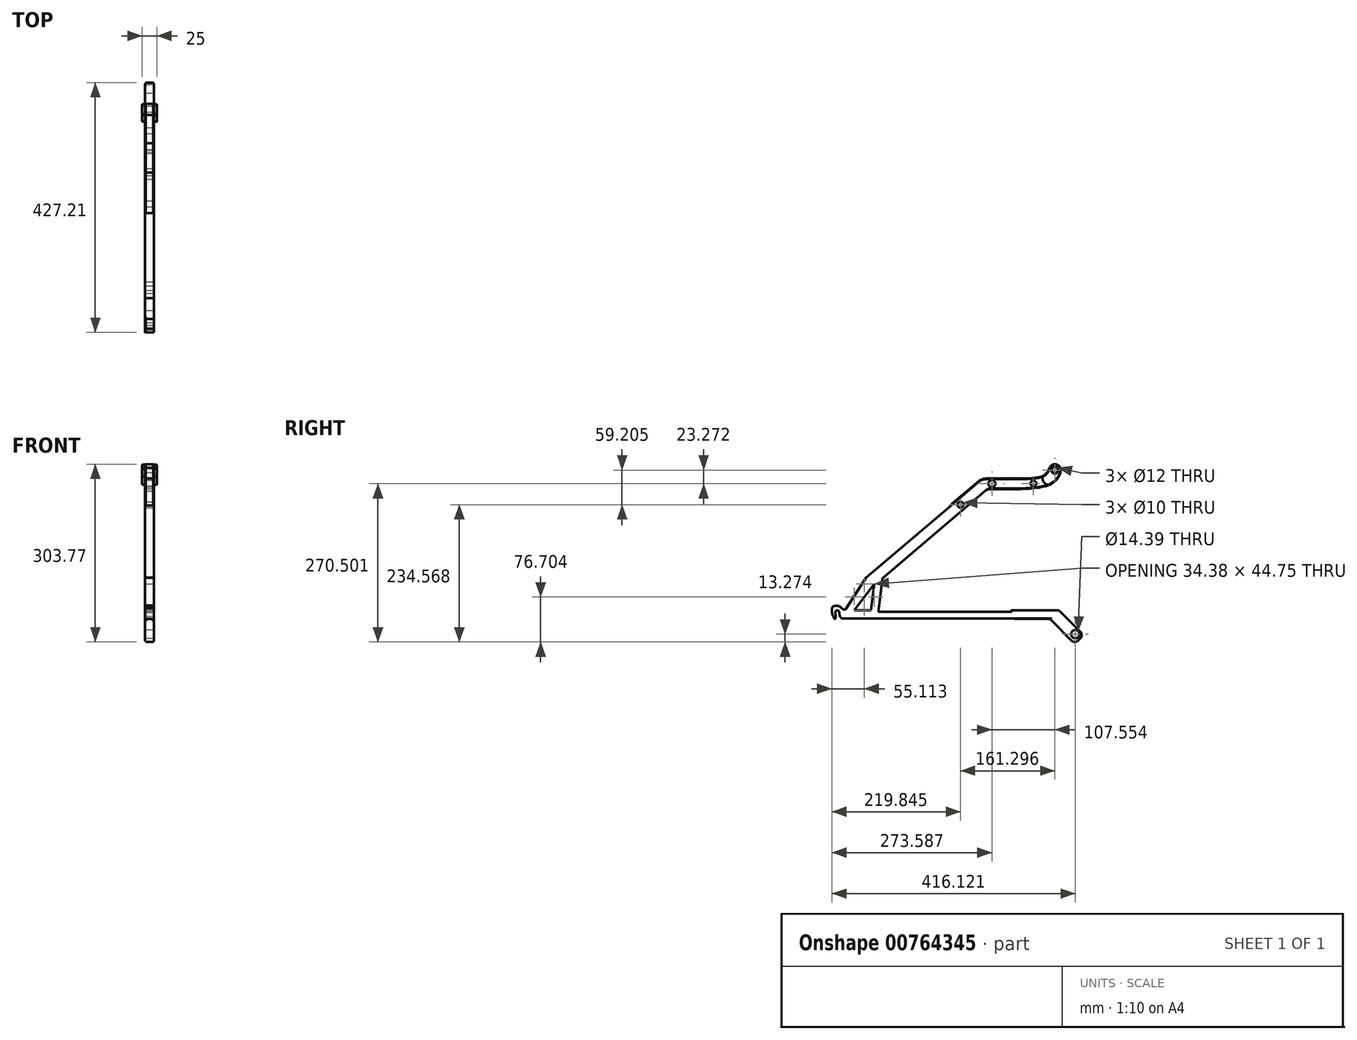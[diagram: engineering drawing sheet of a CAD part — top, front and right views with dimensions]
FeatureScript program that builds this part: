
annotation { "Feature Type Name" : "Feature", "Feature Type Description" : "" }
export const myFeature = defineFeature(function(context is Context, id is Id, definition is map)
    precondition{}
    {
        {
            var Q0;
            Q0=qCreatedBy(makeId("Right.planeOp"),FACE);
            var sketch = newSketch(context, id + "F0", { "sketchPlane" : qUnion([Q0])});
            skLineSegment(sketch, "E0", {"start": v(47.78, 0) * mm, "end": v(315.63, 0) * mm});
            skLineSegment(sketch, "E1", {"start": v(48.64, 41.27) * mm, "end": v(16.93, 0) * mm});
            skLineSegment(sketch, "E2", {"start": v(16.93, 0) * mm, "end": v(47.78, 0) * mm});
            skLineSegment(sketch, "E3.bottom", {"start": v(315.63, 0) * mm, "end": v(16.93, 0) * mm});
            skLineSegment(sketch, "E3.top", {"start": v(315.63, -15) * mm, "end": v(16.93, -15) * mm});
            skLineSegment(sketch, "E3.right", {"start": v(16.93, 0) * mm, "end": v(16.93, -15) * mm});
            skLineSegment(sketch, "E4.left", {"start": v(48.64, 41.27) * mm, "end": v(43.82, 0) * mm});
            skLineSegment(sketch, "E5", {"start": v(48.64, 41.27) * mm, "end": v(35.7, 56.52) * mm});
            skLineSegment(sketch, "E6", {"start": v(239.28, 203) * mm, "end": v(226.34, 218.25) * mm});
            skLineSegment(sketch, "E7", {"start": v(16.93, 0) * mm, "end": v(5.04, 9.14) * mm});
            skLineSegment(sketch, "E8", {"start": v(5.04, 9.14) * mm, "end": v(35.7, 56.52) * mm});
            skLineSegment(sketch, "E9", {"start": v(43.82, 0) * mm, "end": v(58.82, 0) * mm});
            skLineSegment(sketch, "E10", {"start": v(58.82, 0) * mm, "end": v(65.3, 55.4) * mm});
            skLineSegment(sketch, "E11", {"start": v(65.3, 55.4) * mm, "end": v(48.64, 41.27) * mm});
            skFitSpline(sketch, "E12", {"points": [v(226.34, 218.25) * mm, v(234.77, 223.82) * mm, v(251.34, 224.9) * mm], "startDerivative": vector(16.54, 14.26) * mm, "endDerivative": vector(26.5, -0.65) * mm});
            skFitSpline(sketch, "E13", {"points": [v(239.28, 203) * mm, v(245.05, 206.46) * mm, v(251.34, 206.86) * mm], "startDerivative": vector(8.53, 6.98) * mm, "endDerivative": vector(15.33, 0.96) * mm});
            skLineSegment(sketch, "E14.bottom", {"start": v(251.34, 224.9) * mm, "end": v(301.34, 224.9) * mm});
            skLineSegment(sketch, "E14.top", {"start": v(251.34, 206.86) * mm, "end": v(301.34, 206.86) * mm});
            skPoint(sketch, "E15", {"position": v(368.9, 239.44) * mm});
            skPoint(sketch, "E16", {"position": v(358.9, 249.44) * mm});
            skPoint(sketch, "E17", {"position": v(358.9, 229.44) * mm});
            skCircle(sketch, "E18", {"center": v(358.9, 239.44) * mm, "radius": 5 * mm});
            skFitSpline(sketch, "E19", {"points": [v(301.34, 206.86) * mm, v(354.55, 217) * mm, v(368.9, 239.44) * mm], "startDerivative": vector(106.9, 6.32) * mm, "endDerivative": vector(0.42, 60.1) * mm});
            skPoint(sketch, "E20", {"position": v(349.43, 242.67) * mm});
            skFitSpline(sketch, "E21", {"points": [v(301.34, 224.9) * mm, v(340.14, 230.35) * mm, v(349.43, 242.67) * mm], "startDerivative": vector(74.37, 2.6) * mm, "endDerivative": vector(12.8, 33.28) * mm});
            skArc(sketch, "E22", {"start": v(368.9, 239.44) * mm, "mid": v(360.53, 249.3) * mm, "end": v(349.43, 242.67) * mm});
            skCircle(sketch, "E23", {"center": v(322.28, 216.56) * mm, "radius": 5 * mm});
            skCircle(sketch, "E24", {"center": v(251.34, 216.17) * mm, "radius": 6 * mm});
            skLineSegment(sketch, "E25", {"start": v(16.93, -15) * mm, "end": v(5.04, -15) * mm});
            skLineSegment(sketch, "E26", {"start": v(5.04, -15) * mm, "end": v(5.04, 9.14) * mm});
            skLineSegment(sketch, "E27", {"start": v(315.63, -15) * mm, "end": v(315.63, 0) * mm});
            skLineSegment(sketch, "E28", {"start": v(315.63, 0) * mm, "end": v(365.63, 0) * mm});
            skLineSegment(sketch, "E29", {"start": v(365.63, 0) * mm, "end": v(365.63, -15) * mm});
            skLineSegment(sketch, "E30", {"start": v(365.63, -15) * mm, "end": v(315.63, -15) * mm});
            skPoint(sketch, "E31", {"position": v(350.63, -15) * mm});
            skLineSegment(sketch, "E32", {"start": v(365.63, 0) * mm, "end": v(408.06, -42.43) * mm});
            skLineSegment(sketch, "E33", {"start": v(350.63, -15) * mm, "end": v(393.06, -57.43) * mm});
            skLineSegment(sketch, "E34", {"start": v(393.06, -57.43) * mm, "end": v(408.06, -42.43) * mm});
            skPoint(sketch, "E35", {"position": v(358.63, -15) * mm});
            skPoint(sketch, "E36", {"position": v(365.63, -8) * mm});
            skPoint(sketch, "E37", {"position": v(386.84, -21.21) * mm});
            skPoint(sketch, "E38", {"position": v(371.84, -36.21) * mm});
            skLineSegment(sketch, "E39", {"start": v(371.84, -36.21) * mm, "end": v(386.84, -21.21) * mm});
            skCircle(sketch, "E40", {"center": v(393.87, -41.06) * mm, "radius": 7.2 * mm});
            skPoint(sketch, "E41", {"position": v(131.02, 137.39) * mm});
            skPoint(sketch, "E42", {"position": v(143.96, 122.14) * mm});
            skPoint(sketch, "E43", {"position": v(115.77, 124.45) * mm});
            skPoint(sketch, "E44", {"position": v(128.7, 109.2) * mm});
            skPoint(sketch, "E45", {"position": v(159.2, 135.07) * mm});
            skPoint(sketch, "E46", {"position": v(146.27, 150.33) * mm});
            skLineSegment(sketch, "E47", {"start": v(128.7, 109.2) * mm, "end": v(115.77, 124.45) * mm});
            skLineSegment(sketch, "E48", {"start": v(35.7, 56.52) * mm, "end": v(48.64, 41.27) * mm});
            skLineSegment(sketch, "E49", {"start": v(146.27, 150.33) * mm, "end": v(159.2, 135.07) * mm});
            skLineSegment(sketch, "E50", {"start": v(146.27, 150.33) * mm, "end": v(226.34, 218.25) * mm});
            skLineSegment(sketch, "E51", {"start": v(35.7, 56.52) * mm, "end": v(115.77, 124.45) * mm});
            skLineSegment(sketch, "E52", {"start": v(65.3, 55.4) * mm, "end": v(128.7, 109.2) * mm});
            skLineSegment(sketch, "E53", {"start": v(159.2, 135.07) * mm, "end": v(239.28, 203) * mm});
            skLineSegment(sketch, "E54", {"start": v(115.77, 124.45) * mm, "end": v(146.27, 150.33) * mm});
            skLineSegment(sketch, "E55", {"start": v(128.7, 109.2) * mm, "end": v(159.2, 135.07) * mm});
            skSolve(sketch);
        }
        {
            var Q0;
            {var subQ1=sQuery(id+"F0.wireOp",EDGE,"E6");Q0=makeQuery(id+"F0.imprint","IMPRINT",FACE,{"disambiguationData":[TD([[makeQuery(id+"F0.imprint","IMPRINT",EDGE,{"derivedFrom":subQ1}),1.0]])]});}
            var Q1;
            {var subQ1=sQuery(id+"F0.wireOp",EDGE,"E7");Q1=makeQuery(id+"F0.imprint","IMPRINT",FACE,{"disambiguationData":[TD([[makeQuery(id+"F0.imprint","IMPRINT",EDGE,{"derivedFrom":subQ1}),-1.0]])]});}
            var Q2;
            Q2=makeQuery(id+"F0.imprint","IMPRINT",FACE,{"disambiguationData":[TD([[makeQuery(id+"F0.imprint","IMPRINT",EDGE,{"derivedFrom":sQuery(id+"F0.wireOp",EDGE,"E3.right")}),-1.0]])]});
            var Q3;
            Q3=makeQuery(id+"F0.imprint","IMPRINT",FACE,{"disambiguationData":[TD([[makeQuery(id+"F0.imprint","IMPRINT",EDGE,{"derivedFrom":sQuery(id+"F0.wireOp",EDGE,"E3.top")}),-1.0]])]});
            var Q4;
            {var subQ0=sQuery(id+"F0.wireOp",EDGE,"E4.left");Q4=makeQuery(id+"F0.imprint","IMPRINT",FACE,{"disambiguationData":[TD([[makeQuery(id+"F0.imprint","IMPRINT",EDGE,{"derivedFrom":subQ0}),1.0]])]});}
            var Q5;
            {var subQ3=sQuery(id+"F0.wireOp",EDGE,"RTDkQwoI-wCG5-Ql9m-PHR5-vW7OaOIPGGAD.top");Q5=makeQuery(id+"F0.imprint","IMPRINT",FACE,{"disambiguationData":[TD([[makeQuery(id+"F0.imprint","IMPRINT",EDGE,{"derivedFrom":subQ3}),-1.0]])]});}
            var Q6;
            {var subQ1=sQuery(id+"F0.wireOp",EDGE,"E1");var subQ3=sQuery(id+"F0.wireOp",EDGE,"RTDkQwoI-wCG5-Ql9m-PHR5-vW7OaOIPGGAD.left");var subQ4=makeQuery(id+"F0.imprint","INTERSECT",VERTEX,{"derivedFrom":[subQ1,subQ3]});Q6=makeQuery(id+"F0.imprint","IMPRINT",FACE,{"disambiguationData":[TD([[makeQuery(id+"F0.imprint","IMPRINT",EDGE,{"disambiguationData":[TD([[subQ4,-1.0]])],"derivedFrom":subQ3}),-1.0]])]});}
            var Q7;
            {var subQ0=sQuery(id+"F0.wireOp",EDGE,"o3pL6dEJ-hwyi-6mrB-k6X7-aminsl83ahjA");Q7=makeQuery(id+"F0.imprint","IMPRINT",FACE,{"disambiguationData":[TD([[makeQuery(id+"F0.imprint","IMPRINT",EDGE,{"derivedFrom":subQ0}),-1.0]])]});}
            var Q8;
            {var subQ0=sQuery(id+"F0.wireOp",EDGE,"o3pL6dEJ-hwyi-6mrB-k6X7-aminsl83ahjA");Q8=makeQuery(id+"F0.imprint","IMPRINT",FACE,{"disambiguationData":[TD([[makeQuery(id+"F0.imprint","IMPRINT",EDGE,{"derivedFrom":subQ0}),1.0]])]});}
            var Q9;
            Q9=makeQuery(id+"F0.imprint","IMPRINT",FACE,{"disambiguationData":[TD([[makeQuery(id+"F0.imprint","IMPRINT",EDGE,{"derivedFrom":sQuery(id+"F0.wireOp",EDGE,"E6")}),-1.0]])]});
            var Q10;
            Q10=makeQuery(id+"F0.imprint","IMPRINT",FACE,{"disambiguationData":[TD([[makeQuery(id+"F0.imprint","IMPRINT",EDGE,{"derivedFrom":sQuery(id+"F0.wireOp",EDGE,"E14.bottom")}),-1.0]])]});
            var Q11;
            Q11=makeQuery(id+"F0.imprint","IMPRINT",FACE,{"disambiguationData":[TD([[makeQuery(id+"F0.imprint","IMPRINT",EDGE,{"derivedFrom":sQuery(id+"F0.wireOp",EDGE,"E14.right")}),1.0]])]});
            var Q12;
            {var subQ0=sQuery(id+"F0.wireOp",EDGE,"E3.right");Q12=makeQuery(id+"F0.imprint","IMPRINT",FACE,{"disambiguationData":[TD([[makeQuery(id+"F0.imprint","IMPRINT",EDGE,{"derivedFrom":subQ0}),1.0]])]});}
            var Q13;
            {var subQ3=sQuery(id+"F0.wireOp",EDGE,"hnlP5vd8-Fwl7-W3YU-HfNq-rofw2tE7fOju");Q13=makeQuery(id+"F0.imprint","IMPRINT",FACE,{"disambiguationData":[TD([[makeQuery(id+"F0.imprint","IMPRINT",EDGE,{"derivedFrom":subQ3}),-1.0]])]});}
            var Q14;
            {var subQ4=sQuery(id+"F0.wireOp",EDGE,"zAPuBMNa-KC0v-FcAM-JJp2-Pc91iyWnGTPB");Q14=makeQuery(id+"F0.imprint","IMPRINT",FACE,{"disambiguationData":[TD([[makeQuery(id+"F0.imprint","IMPRINT",EDGE,{"derivedFrom":subQ4}),-1.0]])]});}
            var Q15;
            {var subQ0=sQuery(id+"F0.wireOp",EDGE,"E3.left");Q15=makeQuery(id+"F0.imprint","IMPRINT",FACE,{"disambiguationData":[TD([[makeQuery(id+"F0.imprint","IMPRINT",EDGE,{"derivedFrom":subQ0}),1.0]])]});}
            var Q16;
            Q16=makeQuery(id+"F0.imprint","IMPRINT",FACE,{"disambiguationData":[TD([[makeQuery(id+"F0.imprint","IMPRINT",EDGE,{"derivedFrom":sQuery(id+"F0.wireOp",EDGE,"E27")}),-1.0]])]});
            var Q17;
            {var subQ2=sQuery(id+"F0.wireOp",EDGE,"E29");Q17=makeQuery(id+"F0.imprint","IMPRINT",FACE,{"disambiguationData":[TD([[makeQuery(id+"F0.imprint","IMPRINT",EDGE,{"derivedFrom":subQ2}),1.0]])]});}
            var Q18;
            {var subQ0=sQuery(id+"F0.wireOp",EDGE,"E33");var subQ1=sQuery(id+"F0.wireOp",EDGE,"E30");var subQ2=makeQuery(id+"F0.imprint","INTERSECT",VERTEX,{"derivedFrom":[subQ1,subQ0]});Q18=makeQuery(id+"F0.imprint","IMPRINT",FACE,{"disambiguationData":[TD([[makeQuery(id+"F0.imprint","IMPRINT",EDGE,{"disambiguationData":[TD([[subQ2,-1.0]])],"derivedFrom":subQ0}),1.0]])]});}
            var Q19;
            {var subQ5=sQuery(id+"F0.wireOp",EDGE,"E34");Q19=makeQuery(id+"F0.imprint","IMPRINT",FACE,{"disambiguationData":[TD([[makeQuery(id+"F0.imprint","IMPRINT",EDGE,{"derivedFrom":subQ5}),1.0]])]});}
            var Q20;
            Q20=makeQuery(id+"F0.imprint","IMPRINT",FACE,{"disambiguationData":[TD([[makeQuery(id+"F0.imprint","IMPRINT",EDGE,{"derivedFrom":sQuery(id+"F0.wireOp",EDGE,"E11")}),-1.0]])]});
            var Q21;
            Q21=makeQuery(id+"F0.imprint","IMPRINT",FACE,{"disambiguationData":[TD([[makeQuery(id+"F0.imprint","IMPRINT",EDGE,{"derivedFrom":sQuery(id+"F0.wireOp",EDGE,"E49")}),1.0]])]});
            var Q22;
            Q22=makeQuery(id+"F0.imprint","IMPRINT",FACE,{"disambiguationData":[TD([[makeQuery(id+"F0.imprint","IMPRINT",EDGE,{"derivedFrom":sQuery(id+"F0.wireOp",EDGE,"E47")}),-1.0]])]});
            extrude(context, id + "F1", {"entities" : qUnion([Q0, Q1, Q2, Q3, Q4, Q5, Q6, Q7, Q8, Q9, Q10, Q11, Q12, Q13, Q14, Q15, Q16, Q17, Q18, Q19, Q20, Q21, Q22]), "depth" : 15 * mm, "offsetDistance" : 25 * mm});
        }
        {
            var Q0;
            {var subQ0=sQuery(id+"F0.wireOp",EDGE,"E3.bottom");Q0=makeQuery(id+"F1.opExtrude","CAP_EDGE",EDGE,{"disambiguationData":[OSD([subQ0]),TDD([makeQuery(id+"F0.imprint","IMPRINT",EDGE,{"disambiguationData":[TD([[makeQuery(id+"F0.imprint","INTERSECT",VERTEX,{"derivedFrom":[subQ0,sQuery(id+"F0.wireOp",EDGE,"E3.left")]}),-1.0]])],"derivedFrom":subQ0})])],"isStart":false});}
            var Q1;
            {var subQ0=sQuery(id+"F0.wireOp",EDGE,"E3.bottom");Q1=makeQuery(id+"F1.opExtrude","CAP_EDGE",EDGE,{"disambiguationData":[OSD([subQ0]),TDD([makeQuery(id+"F0.imprint","IMPRINT",EDGE,{"disambiguationData":[TD([[makeQuery(id+"F0.imprint","INTERSECT",VERTEX,{"derivedFrom":[subQ0,sQuery(id+"F0.wireOp",EDGE,"E3.left")]}),-1.0]])],"derivedFrom":subQ0})])],"isStart":true});}
            var Q2;
            Q2=makeQuery(id+"F1.opExtrude","CAP_EDGE",EDGE,{"disambiguationData":[OSD([sQuery(id+"F0.wireOp",EDGE,"E3.top")])],"isStart":true});
            var Q3;
            Q3=makeQuery(id+"F1.opExtrude","CAP_EDGE",EDGE,{"disambiguationData":[OSD([sQuery(id+"F0.wireOp",EDGE,"E3.top")])],"isStart":false});
            var Q4;
            Q4=makeQuery(id+"F1.opExtrude","CAP_EDGE",EDGE,{"disambiguationData":[OSD([sQuery(id+"F0.wireOp",EDGE,"E3.left")])],"isStart":false});
            var Q5;
            Q5=makeQuery(id+"F1.opExtrude","SWEPT_EDGE",EDGE,{"disambiguationData":[OSD([sQuery(id+"F0.wireOp",EDGE,"E3.bottom"),sQuery(id+"F0.wireOp",EDGE,"E3.left")])]});
            var Q6;
            Q6=makeQuery(id+"F1.opExtrude","CAP_EDGE",EDGE,{"disambiguationData":[OSD([sQuery(id+"F0.wireOp",EDGE,"E3.left")])],"isStart":true});
            var Q7;
            Q7=makeQuery(id+"F1.opExtrude","SWEPT_EDGE",EDGE,{"disambiguationData":[OSD([sQuery(id+"F0.wireOp",EDGE,"E3.top"),sQuery(id+"F0.wireOp",EDGE,"E3.left")])]});
            var Q8;
            Q8=makeQuery(id+"F1.opExtrude","CAP_EDGE",EDGE,{"disambiguationData":[OSD([sQuery(id+"F0.wireOp",EDGE,"d41c5ef0-c10e-4e75-b374-802d414c0d57")])],"isStart":false});
            var Q9;
            Q9=makeQuery(id+"F1.opExtrude","CAP_EDGE",EDGE,{"disambiguationData":[OSD([sQuery(id+"F0.wireOp",EDGE,"d41c5ef0-c10e-4e75-b374-802d414c0d57")])],"isStart":true});
            var Q10;
            Q10=makeQuery(id+"F1.opExtrude","CAP_EDGE",EDGE,{"disambiguationData":[OSD([sQuery(id+"F0.wireOp",EDGE,"E1")])],"isStart":false});
            var Q11;
            Q11=makeQuery(id+"F1.opExtrude","CAP_EDGE",EDGE,{"disambiguationData":[OSD([sQuery(id+"F0.wireOp",EDGE,"E4.left")])],"isStart":false});
            var Q12;
            {var subQ0=sQuery(id+"F0.wireOp",EDGE,"E3.bottom");Q12=makeQuery(id+"F1.opExtrude","CAP_EDGE",EDGE,{"disambiguationData":[OSD([subQ0]),TDD([makeQuery(id+"F0.imprint","IMPRINT",EDGE,{"disambiguationData":[TD([[makeQuery(id+"F0.imprint","INTERSECT",VERTEX,{"derivedFrom":[subQ0,sQuery(id+"F0.wireOp",EDGE,"E4.left"),sQuery(id+"F0.wireOp",EDGE,"E9")]}),-1.0]])],"derivedFrom":subQ0})])],"isStart":false});}
            var Q13;
            Q13=makeQuery(id+"F1.opExtrude","CAP_EDGE",EDGE,{"disambiguationData":[OSD([sQuery(id+"F0.wireOp",EDGE,"E10")])],"isStart":false});
            var Q14;
            Q14=makeQuery(id+"F1.opExtrude","CAP_EDGE",EDGE,{"disambiguationData":[OSD([sQuery(id+"F0.wireOp",EDGE,"E8")])],"isStart":false});
            var Q15;
            Q15=makeQuery(id+"F1.opExtrude","CAP_EDGE",EDGE,{"disambiguationData":[OSD([sQuery(id+"F0.wireOp",EDGE,"E8")])],"isStart":true});
            var Q16;
            Q16=makeQuery(id+"F1.opExtrude","CAP_EDGE",EDGE,{"disambiguationData":[OSD([sQuery(id+"F0.wireOp",EDGE,"E1")])],"isStart":true});
            var Q17;
            Q17=makeQuery(id+"F1.opExtrude","CAP_EDGE",EDGE,{"disambiguationData":[OSD([sQuery(id+"F0.wireOp",EDGE,"E4.left")])],"isStart":true});
            var Q18;
            {var subQ0=sQuery(id+"F0.wireOp",EDGE,"E3.bottom");Q18=makeQuery(id+"F1.opExtrude","CAP_EDGE",EDGE,{"disambiguationData":[OSD([subQ0]),TDD([makeQuery(id+"F0.imprint","IMPRINT",EDGE,{"disambiguationData":[TD([[makeQuery(id+"F0.imprint","INTERSECT",VERTEX,{"derivedFrom":[subQ0,sQuery(id+"F0.wireOp",EDGE,"E4.left"),sQuery(id+"F0.wireOp",EDGE,"E9")]}),-1.0]])],"derivedFrom":subQ0})])],"isStart":true});}
            var Q19;
            Q19=makeQuery(id+"F1.opExtrude","CAP_EDGE",EDGE,{"disambiguationData":[OSD([sQuery(id+"F0.wireOp",EDGE,"E10")])],"isStart":true});
            var Q20;
            Q20=makeQuery(id+"F1.opExtrude","CAP_EDGE",EDGE,{"disambiguationData":[OSD([sQuery(id+"F0.wireOp",EDGE,"uIqcDY9T-Jbxf-aRt4-gg0R-6jHuYA81VSVm")])],"isStart":true});
            var Q21;
            Q21=makeQuery(id+"F1.opExtrude","CAP_EDGE",EDGE,{"disambiguationData":[OSD([sQuery(id+"F0.wireOp",EDGE,"uIqcDY9T-Jbxf-aRt4-gg0R-6jHuYA81VSVm")])],"isStart":false});
            var Q22;
            Q22=makeQuery(id+"F1.opExtrude","CAP_EDGE",EDGE,{"disambiguationData":[OSD([sQuery(id+"F0.wireOp",EDGE,"rEmcZTTS-8Wlh-duEK-OSmW-KXRGUTnN0HfS")])],"isStart":true});
            var Q23;
            Q23=makeQuery(id+"F1.opExtrude","CAP_EDGE",EDGE,{"disambiguationData":[OSD([sQuery(id+"F0.wireOp",EDGE,"rEmcZTTS-8Wlh-duEK-OSmW-KXRGUTnN0HfS")])],"isStart":false});
            var Q24;
            Q24=makeQuery(id+"F1.opExtrude","CAP_EDGE",EDGE,{"disambiguationData":[OSD([sQuery(id+"F0.wireOp",EDGE,"E12")])],"isStart":false});
            var Q25;
            Q25=makeQuery(id+"F1.opExtrude","CAP_EDGE",EDGE,{"disambiguationData":[OSD([sQuery(id+"F0.wireOp",EDGE,"E12")])],"isStart":true});
            var Q26;
            Q26=makeQuery(id+"F1.opExtrude","CAP_EDGE",EDGE,{"disambiguationData":[OSD([sQuery(id+"F0.wireOp",EDGE,"E14.bottom")])],"isStart":false});
            var Q27;
            Q27=makeQuery(id+"F1.opExtrude","CAP_EDGE",EDGE,{"disambiguationData":[OSD([sQuery(id+"F0.wireOp",EDGE,"E14.bottom")])],"isStart":true});
            var Q28;
            Q28=makeQuery(id+"F1.opExtrude","CAP_EDGE",EDGE,{"disambiguationData":[OSD([sQuery(id+"F0.wireOp",EDGE,"E21")])],"isStart":false});
            var Q29;
            Q29=makeQuery(id+"F1.opExtrude","CAP_EDGE",EDGE,{"disambiguationData":[OSD([sQuery(id+"F0.wireOp",EDGE,"E21")])],"isStart":true});
            var Q30;
            Q30=makeQuery(id+"F1.opExtrude","CAP_EDGE",EDGE,{"disambiguationData":[OSD([sQuery(id+"F0.wireOp",EDGE,"E13")])],"isStart":false});
            var Q31;
            Q31=makeQuery(id+"F1.opExtrude","CAP_EDGE",EDGE,{"disambiguationData":[OSD([sQuery(id+"F0.wireOp",EDGE,"E14.top")])],"isStart":false});
            var Q32;
            Q32=makeQuery(id+"F1.opExtrude","CAP_EDGE",EDGE,{"disambiguationData":[OSD([sQuery(id+"F0.wireOp",EDGE,"E19")])],"isStart":false});
            var Q33;
            Q33=makeQuery(id+"F1.opExtrude","CAP_EDGE",EDGE,{"disambiguationData":[OSD([sQuery(id+"F0.wireOp",EDGE,"E22")])],"isStart":false});
            var Q34;
            Q34=makeQuery(id+"F1.opExtrude","CAP_EDGE",EDGE,{"disambiguationData":[OSD([sQuery(id+"F0.wireOp",EDGE,"E18")])],"isStart":false});
            var Q35;
            Q35=makeQuery(id+"F1.opExtrude","CAP_EDGE",EDGE,{"disambiguationData":[OSD([sQuery(id+"F0.wireOp",EDGE,"E22")])],"isStart":true});
            var Q36;
            Q36=makeQuery(id+"F1.opExtrude","CAP_EDGE",EDGE,{"disambiguationData":[OSD([sQuery(id+"F0.wireOp",EDGE,"E18")])],"isStart":true});
            var Q37;
            Q37=makeQuery(id+"F1.opExtrude","CAP_EDGE",EDGE,{"disambiguationData":[OSD([sQuery(id+"F0.wireOp",EDGE,"E19")])],"isStart":true});
            var Q38;
            Q38=makeQuery(id+"F1.opExtrude","CAP_EDGE",EDGE,{"disambiguationData":[OSD([sQuery(id+"F0.wireOp",EDGE,"E14.top")])],"isStart":true});
            var Q39;
            Q39=makeQuery(id+"F1.opExtrude","CAP_EDGE",EDGE,{"disambiguationData":[OSD([sQuery(id+"F0.wireOp",EDGE,"E13")])],"isStart":true});
            chamfer(context, id + "F2", {"entities" : qUnion([Q0, Q1, Q2, Q3, Q4, Q5, Q6, Q7, Q8, Q9, Q10, Q11, Q12, Q13, Q14, Q15, Q16, Q17, Q18, Q19, Q20, Q21, Q22, Q23, Q24, Q25, Q26, Q27, Q28, Q29, Q30, Q31, Q32, Q33, Q34, Q35, Q36, Q37, Q38, Q39]), "width" : 1 * mm, "tangentPropagation" : true});
        }
        {
            var Q0;
            Q0=makeQuery(id+"F1.opExtrude","SWEPT_EDGE",EDGE,{"disambiguationData":[OSD([sQuery(id+"F0.wireOp",EDGE,"E3.bottom"),sQuery(id+"F0.wireOp",EDGE,"E9"),sQuery(id+"F0.wireOp",EDGE,"E10")])]});
            var Q1;
            Q1=makeQuery(id+"F1.opExtrude","SWEPT_EDGE",EDGE,{"disambiguationData":[OSD([sQuery(id+"F0.wireOp",EDGE,"uIqcDY9T-Jbxf-aRt4-gg0R-6jHuYA81VSVm"),sQuery(id+"F0.wireOp",EDGE,"E10"),sQuery(id+"F0.wireOp",EDGE,"E11")])]});
            fillet(context, id + "F3", {"entities" : qUnion([Q0, Q1]), "radius" : 2 * mm, "tangentPropagation" : true, "allowEdgeOverflow" : false});
        }
        {
            var Q0;
            Q0=makeQuery(id+"F1.opExtrude","SWEPT_EDGE",EDGE,{"disambiguationData":[OSD([sQuery(id+"F0.wireOp",EDGE,"E3.bottom"),sQuery(id+"F0.wireOp",EDGE,"E4.left"),sQuery(id+"F0.wireOp",EDGE,"E9")])]});
            var Q1;
            Q1=makeQuery(id+"F1.opExtrude","SWEPT_EDGE",EDGE,{"disambiguationData":[OSD([sQuery(id+"F0.wireOp",EDGE,"E1"),sQuery(id+"F0.wireOp",EDGE,"E3.bottom"),sQuery(id+"F0.wireOp",EDGE,"E3.right"),sQuery(id+"F0.wireOp",EDGE,"E7")])]});
            var Q2;
            Q2=makeQuery(id+"F1.opExtrude","SWEPT_EDGE",EDGE,{"disambiguationData":[OSD([sQuery(id+"F0.wireOp",EDGE,"E1"),sQuery(id+"F0.wireOp",EDGE,"E4.left"),sQuery(id+"F0.wireOp",EDGE,"E5"),sQuery(id+"F0.wireOp",EDGE,"E11")])]});
            fillet(context, id + "F4", {"entities" : qUnion([Q0, Q1, Q2]), "radius" : 1 * mm, "tangentPropagation" : true, "allowEdgeOverflow" : false});
        }
        {
            var Q0;
            Q0=makeQuery(id+"F1.opExtrude","SWEPT_FACE",FACE,{"disambiguationData":[OSD([sQuery(id+"F0.wireOp",EDGE,"E26")])]});
            var sketch = newSketch(context, id + "F5", { "sketchPlane" : qUnion([Q0])});
            skLineSegment(sketch, "E56.bottom", {"start": v(0, -15) * mm, "end": v(15, -15) * mm});
            skLineSegment(sketch, "E56.top", {"start": v(0, 9.14) * mm, "end": v(15, 9.14) * mm});
            skLineSegment(sketch, "E56.left", {"start": v(0, -15) * mm, "end": v(0, 9.14) * mm});
            skLineSegment(sketch, "E56.right", {"start": v(15, -15) * mm, "end": v(15, 9.14) * mm});
            skSolve(sketch);
        }
        {
            var Q0;
            Q0 = qSketchRegion(id + "F5", true);
            extrude(context, id + "F6", {"entities" : qUnion([Q0]), "operationType" : NewBodyOperationType.ADD, "depth" : 35 * mm, "offsetDistance" : 25 * mm});
        }
        {
            var Q0;
            Q0=makeQuery(id+"F6.boolean.opBoolean","MERGE",FACE,{"derivedFrom":[makeQuery(id+"F2.opChamfer","SPLIT",FACE,{"disambiguationData":[OD(0.0)],"derivedFrom":makeQuery(id+"F1.opExtrude","CAP_FACE",FACE,{"disambiguationData":[OSD([sQuery(id+"F0.wireOp",EDGE,"uIqcDY9T-Jbxf-aRt4-gg0R-6jHuYA81VSVm"),sQuery(id+"F0.wireOp",EDGE,"E1"),sQuery(id+"F0.wireOp",EDGE,"E3.bottom"),sQuery(id+"F0.wireOp",EDGE,"E3.top"),sQuery(id+"F0.wireOp",EDGE,"E3.left"),sQuery(id+"F0.wireOp",EDGE,"E4.left"),sQuery(id+"F0.wireOp",EDGE,"rEmcZTTS-8Wlh-duEK-OSmW-KXRGUTnN0HfS"),sQuery(id+"F0.wireOp",EDGE,"E8"),sQuery(id+"F0.wireOp",EDGE,"E10"),sQuery(id+"F0.wireOp",EDGE,"E12"),sQuery(id+"F0.wireOp",EDGE,"E13"),sQuery(id+"F0.wireOp",EDGE,"E14.bottom"),sQuery(id+"F0.wireOp",EDGE,"E14.top"),sQuery(id+"F0.wireOp",EDGE,"E18"),sQuery(id+"F0.wireOp",EDGE,"E19"),sQuery(id+"F0.wireOp",EDGE,"E21"),sQuery(id+"F0.wireOp",EDGE,"E22"),sQuery(id+"F0.wireOp",EDGE,"E23"),sQuery(id+"F0.wireOp",EDGE,"E24"),sQuery(id+"F0.wireOp",EDGE,"E25"),sQuery(id+"F0.wireOp",EDGE,"E26")])],"isStart":false})}),makeQuery(id+"F6.opExtrude","SWEPT_FACE",FACE,{"disambiguationData":[OSD([sQuery(id+"F5.wireOp",EDGE,"E56.right")])]})]});
            var sketch = newSketch(context, id + "F7", { "sketchPlane" : qUnion([Q0])});
            skLineSegment(sketch, "E57", {"start": v(5.04, 7.3) * mm, "end": v(1.23, 1.42) * mm});
            skPoint(sketch, "E58", {"position": v(-15.29, -15) * mm});
            skPoint(sketch, "E59", {"position": v(-8.29, -15) * mm});
            skFitSpline(sketch, "E60", {"points": [v(-15.81, -10.33) * mm, v(-16.74, -15) * mm, v(-20.68, -11.17) * mm], "startDerivative": vector(3.5, -16.33) * mm, "endDerivative": vector(-10.01, 17.22) * mm});
            skArc(sketch, "E61", {"start": v(-9.8, -2.74) * mm, "mid": v(-13.78, -0.75) * mm, "end": v(-16.49, -4.3) * mm});
            skFitSpline(sketch, "E62", {"points": [v(-23.08, 0.68) * mm, v(-23.08, -3.12) * mm, v(-20.68, -11.17) * mm], "startDerivative": vector(0.94, -17.18) * mm, "endDerivative": vector(7.79, -14.34) * mm});
            skLineSegment(sketch, "E63", {"start": v(-16.49, -4.3) * mm, "end": v(-15.81, -10.33) * mm});
            skFitSpline(sketch, "E64", {"points": [v(-9.8, -2.74) * mm, v(-6.92, -12.83) * mm, v(5.04, -15) * mm], "startDerivative": vector(3.63, -23.4) * mm, "endDerivative": vector(29.15, 0) * mm});
            skArc(sketch, "E65", {"start": v(-15.82, 7.7) * mm, "mid": v(-20.83, 5.61) * mm, "end": v(-23.08, 0.68) * mm});
            skFitSpline(sketch, "E66", {"points": [v(1.23, 1.42) * mm, v(-6.2, 4.2) * mm, v(-15.82, 7.7) * mm], "startDerivative": vector(-16.53, -11.89) * mm, "endDerivative": vector(-29.61, -1.65) * mm});
            skLineSegment(sketch, "E67", {"start": v(5.04, 7.3) * mm, "end": v(5.04, -15) * mm});
            skSolve(sketch);
        }
        {
            var Q0;
            Q0=makeQuery(id+"F7.imprint","IMPRINT",FACE,{"disambiguationData":[TD([[makeQuery(id+"F7.imprint","IMPRINT",EDGE,{"derivedFrom":sQuery(id+"F7.wireOp",EDGE,"E57")}),-1.0]])]});
            var Q1;
            {var subQ1=sQuery(id+"F7.wireOp",EDGE,"E61");Q1=makeQuery(id+"F7.imprint","IMPRINT",FACE,{"disambiguationData":[TD([[makeQuery(id+"F7.imprint","IMPRINT",EDGE,{"derivedFrom":subQ1}),1.0]])]});}
            extrude(context, id + "F8", {"entities" : qUnion([Q0, Q1]), "operationType" : NewBodyOperationType.REMOVE, "oppositeDirection" : true, "depth" : 25 * mm, "offsetDistance" : 25 * mm});
        }
        {
            var Q0;
            Q0=makeQuery(id+"F8.boolean.opBoolean","COPY",EDGE,{"derivedFrom":makeQuery(id+"F8.opExtrude","CAP_EDGE",EDGE,{"disambiguationData":[OSD([sQuery(id+"F7.wireOp",EDGE,"E66")])],"isStart":true})});
            var Q1;
            Q1=makeQuery(id+"F8.boolean.opBoolean","INTERSECT",EDGE,{"derivedFrom":[makeQuery(id+"F6.boolean.opBoolean","MERGE",FACE,{"derivedFrom":[makeQuery(id+"F2.opChamfer","SPLIT",FACE,{"disambiguationData":[OD(0.0)],"derivedFrom":makeQuery(id+"F1.opExtrude","CAP_FACE",FACE,{"disambiguationData":[OSD([sQuery(id+"F0.wireOp",EDGE,"uIqcDY9T-Jbxf-aRt4-gg0R-6jHuYA81VSVm"),sQuery(id+"F0.wireOp",EDGE,"E1"),sQuery(id+"F0.wireOp",EDGE,"E3.bottom"),sQuery(id+"F0.wireOp",EDGE,"E3.top"),sQuery(id+"F0.wireOp",EDGE,"E3.left"),sQuery(id+"F0.wireOp",EDGE,"E4.left"),sQuery(id+"F0.wireOp",EDGE,"rEmcZTTS-8Wlh-duEK-OSmW-KXRGUTnN0HfS"),sQuery(id+"F0.wireOp",EDGE,"E8"),sQuery(id+"F0.wireOp",EDGE,"E10"),sQuery(id+"F0.wireOp",EDGE,"E12"),sQuery(id+"F0.wireOp",EDGE,"E13"),sQuery(id+"F0.wireOp",EDGE,"E14.bottom"),sQuery(id+"F0.wireOp",EDGE,"E14.top"),sQuery(id+"F0.wireOp",EDGE,"E18"),sQuery(id+"F0.wireOp",EDGE,"E19"),sQuery(id+"F0.wireOp",EDGE,"E21"),sQuery(id+"F0.wireOp",EDGE,"E22"),sQuery(id+"F0.wireOp",EDGE,"E23"),sQuery(id+"F0.wireOp",EDGE,"E24"),sQuery(id+"F0.wireOp",EDGE,"E25"),sQuery(id+"F0.wireOp",EDGE,"E26")])],"isStart":true})}),makeQuery(id+"F6.opExtrude","SWEPT_FACE",FACE,{"disambiguationData":[OSD([sQuery(id+"F5.wireOp",EDGE,"E56.left")])]})]}),makeQuery(id+"F8.opExtrude","SWEPT_FACE",FACE,{"disambiguationData":[OSD([sQuery(id+"F7.wireOp",EDGE,"E66")])]})]});
            var Q2;
            Q2=makeQuery(id+"F8.boolean.opBoolean","COPY",EDGE,{"derivedFrom":makeQuery(id+"F8.opExtrude","CAP_EDGE",EDGE,{"disambiguationData":[OSD([sQuery(id+"F7.wireOp",EDGE,"E65")])],"isStart":true})});
            var Q3;
            Q3=makeQuery(id+"F8.boolean.opBoolean","INTERSECT",EDGE,{"derivedFrom":[makeQuery(id+"F6.boolean.opBoolean","MERGE",FACE,{"derivedFrom":[makeQuery(id+"F2.opChamfer","SPLIT",FACE,{"disambiguationData":[OD(0.0)],"derivedFrom":makeQuery(id+"F1.opExtrude","CAP_FACE",FACE,{"disambiguationData":[OSD([sQuery(id+"F0.wireOp",EDGE,"uIqcDY9T-Jbxf-aRt4-gg0R-6jHuYA81VSVm"),sQuery(id+"F0.wireOp",EDGE,"E1"),sQuery(id+"F0.wireOp",EDGE,"E3.bottom"),sQuery(id+"F0.wireOp",EDGE,"E3.top"),sQuery(id+"F0.wireOp",EDGE,"E3.left"),sQuery(id+"F0.wireOp",EDGE,"E4.left"),sQuery(id+"F0.wireOp",EDGE,"rEmcZTTS-8Wlh-duEK-OSmW-KXRGUTnN0HfS"),sQuery(id+"F0.wireOp",EDGE,"E8"),sQuery(id+"F0.wireOp",EDGE,"E10"),sQuery(id+"F0.wireOp",EDGE,"E12"),sQuery(id+"F0.wireOp",EDGE,"E13"),sQuery(id+"F0.wireOp",EDGE,"E14.bottom"),sQuery(id+"F0.wireOp",EDGE,"E14.top"),sQuery(id+"F0.wireOp",EDGE,"E18"),sQuery(id+"F0.wireOp",EDGE,"E19"),sQuery(id+"F0.wireOp",EDGE,"E21"),sQuery(id+"F0.wireOp",EDGE,"E22"),sQuery(id+"F0.wireOp",EDGE,"E23"),sQuery(id+"F0.wireOp",EDGE,"E24"),sQuery(id+"F0.wireOp",EDGE,"E25"),sQuery(id+"F0.wireOp",EDGE,"E26")])],"isStart":true})}),makeQuery(id+"F6.opExtrude","SWEPT_FACE",FACE,{"disambiguationData":[OSD([sQuery(id+"F5.wireOp",EDGE,"E56.left")])]})]}),makeQuery(id+"F8.opExtrude","SWEPT_FACE",FACE,{"disambiguationData":[OSD([sQuery(id+"F7.wireOp",EDGE,"E65")])]})]});
            var Q4;
            Q4=makeQuery(id+"F8.boolean.opBoolean","COPY",EDGE,{"derivedFrom":makeQuery(id+"F8.opExtrude","CAP_EDGE",EDGE,{"disambiguationData":[OSD([sQuery(id+"F7.wireOp",EDGE,"E57")])],"isStart":true})});
            var Q5;
            Q5=makeQuery(id+"F8.boolean.opBoolean","INTERSECT",EDGE,{"derivedFrom":[makeQuery(id+"F6.boolean.opBoolean","MERGE",FACE,{"derivedFrom":[makeQuery(id+"F2.opChamfer","SPLIT",FACE,{"disambiguationData":[OD(0.0)],"derivedFrom":makeQuery(id+"F1.opExtrude","CAP_FACE",FACE,{"disambiguationData":[OSD([sQuery(id+"F0.wireOp",EDGE,"uIqcDY9T-Jbxf-aRt4-gg0R-6jHuYA81VSVm"),sQuery(id+"F0.wireOp",EDGE,"E1"),sQuery(id+"F0.wireOp",EDGE,"E3.bottom"),sQuery(id+"F0.wireOp",EDGE,"E3.top"),sQuery(id+"F0.wireOp",EDGE,"E3.left"),sQuery(id+"F0.wireOp",EDGE,"E4.left"),sQuery(id+"F0.wireOp",EDGE,"rEmcZTTS-8Wlh-duEK-OSmW-KXRGUTnN0HfS"),sQuery(id+"F0.wireOp",EDGE,"E8"),sQuery(id+"F0.wireOp",EDGE,"E10"),sQuery(id+"F0.wireOp",EDGE,"E12"),sQuery(id+"F0.wireOp",EDGE,"E13"),sQuery(id+"F0.wireOp",EDGE,"E14.bottom"),sQuery(id+"F0.wireOp",EDGE,"E14.top"),sQuery(id+"F0.wireOp",EDGE,"E18"),sQuery(id+"F0.wireOp",EDGE,"E19"),sQuery(id+"F0.wireOp",EDGE,"E21"),sQuery(id+"F0.wireOp",EDGE,"E22"),sQuery(id+"F0.wireOp",EDGE,"E23"),sQuery(id+"F0.wireOp",EDGE,"E24"),sQuery(id+"F0.wireOp",EDGE,"E25"),sQuery(id+"F0.wireOp",EDGE,"E26")])],"isStart":true})}),makeQuery(id+"F6.opExtrude","SWEPT_FACE",FACE,{"disambiguationData":[OSD([sQuery(id+"F5.wireOp",EDGE,"E56.left")])]})]}),makeQuery(id+"F8.opExtrude","SWEPT_FACE",FACE,{"disambiguationData":[OSD([sQuery(id+"F7.wireOp",EDGE,"E57")])]})]});
            var Q6;
            Q6=makeQuery(id+"F8.boolean.opBoolean","COPY",EDGE,{"derivedFrom":makeQuery(id+"F8.opExtrude","CAP_EDGE",EDGE,{"disambiguationData":[OSD([sQuery(id+"F7.wireOp",EDGE,"E62")])],"isStart":true})});
            var Q7;
            Q7=makeQuery(id+"F8.boolean.opBoolean","COPY",FACE,{"derivedFrom":makeQuery(id+"F8.opExtrude","SWEPT_FACE",FACE,{"disambiguationData":[OSD([sQuery(id+"F7.wireOp",EDGE,"E62")])]})});
            var Q8;
            Q8=makeQuery(id+"F8.boolean.opBoolean","COPY",EDGE,{"derivedFrom":makeQuery(id+"F8.opExtrude","CAP_EDGE",EDGE,{"disambiguationData":[OSD([sQuery(id+"F7.wireOp",EDGE,"E61")])],"isStart":true})});
            var Q9;
            Q9=makeQuery(id+"F8.boolean.opBoolean","INTERSECT",EDGE,{"derivedFrom":[makeQuery(id+"F6.boolean.opBoolean","MERGE",FACE,{"derivedFrom":[makeQuery(id+"F2.opChamfer","SPLIT",FACE,{"disambiguationData":[OD(0.0)],"derivedFrom":makeQuery(id+"F1.opExtrude","CAP_FACE",FACE,{"disambiguationData":[OSD([sQuery(id+"F0.wireOp",EDGE,"uIqcDY9T-Jbxf-aRt4-gg0R-6jHuYA81VSVm"),sQuery(id+"F0.wireOp",EDGE,"E1"),sQuery(id+"F0.wireOp",EDGE,"E3.bottom"),sQuery(id+"F0.wireOp",EDGE,"E3.top"),sQuery(id+"F0.wireOp",EDGE,"E3.left"),sQuery(id+"F0.wireOp",EDGE,"E4.left"),sQuery(id+"F0.wireOp",EDGE,"rEmcZTTS-8Wlh-duEK-OSmW-KXRGUTnN0HfS"),sQuery(id+"F0.wireOp",EDGE,"E8"),sQuery(id+"F0.wireOp",EDGE,"E10"),sQuery(id+"F0.wireOp",EDGE,"E12"),sQuery(id+"F0.wireOp",EDGE,"E13"),sQuery(id+"F0.wireOp",EDGE,"E14.bottom"),sQuery(id+"F0.wireOp",EDGE,"E14.top"),sQuery(id+"F0.wireOp",EDGE,"E18"),sQuery(id+"F0.wireOp",EDGE,"E19"),sQuery(id+"F0.wireOp",EDGE,"E21"),sQuery(id+"F0.wireOp",EDGE,"E22"),sQuery(id+"F0.wireOp",EDGE,"E23"),sQuery(id+"F0.wireOp",EDGE,"E24"),sQuery(id+"F0.wireOp",EDGE,"E25"),sQuery(id+"F0.wireOp",EDGE,"E26")])],"isStart":true})}),makeQuery(id+"F6.opExtrude","SWEPT_FACE",FACE,{"disambiguationData":[OSD([sQuery(id+"F5.wireOp",EDGE,"E56.left")])]})]}),makeQuery(id+"F8.opExtrude","SWEPT_FACE",FACE,{"disambiguationData":[OSD([sQuery(id+"F7.wireOp",EDGE,"E61")])]})]});
            var Q10;
            Q10=makeQuery(id+"F8.boolean.opBoolean","COPY",EDGE,{"derivedFrom":makeQuery(id+"F8.opExtrude","CAP_EDGE",EDGE,{"disambiguationData":[OSD([sQuery(id+"F7.wireOp",EDGE,"E64")])],"isStart":true})});
            var Q11;
            Q11=makeQuery(id+"F8.boolean.opBoolean","INTERSECT",EDGE,{"derivedFrom":[makeQuery(id+"F6.boolean.opBoolean","MERGE",FACE,{"derivedFrom":[makeQuery(id+"F2.opChamfer","SPLIT",FACE,{"disambiguationData":[OD(0.0)],"derivedFrom":makeQuery(id+"F1.opExtrude","CAP_FACE",FACE,{"disambiguationData":[OSD([sQuery(id+"F0.wireOp",EDGE,"uIqcDY9T-Jbxf-aRt4-gg0R-6jHuYA81VSVm"),sQuery(id+"F0.wireOp",EDGE,"E1"),sQuery(id+"F0.wireOp",EDGE,"E3.bottom"),sQuery(id+"F0.wireOp",EDGE,"E3.top"),sQuery(id+"F0.wireOp",EDGE,"E3.left"),sQuery(id+"F0.wireOp",EDGE,"E4.left"),sQuery(id+"F0.wireOp",EDGE,"rEmcZTTS-8Wlh-duEK-OSmW-KXRGUTnN0HfS"),sQuery(id+"F0.wireOp",EDGE,"E8"),sQuery(id+"F0.wireOp",EDGE,"E10"),sQuery(id+"F0.wireOp",EDGE,"E12"),sQuery(id+"F0.wireOp",EDGE,"E13"),sQuery(id+"F0.wireOp",EDGE,"E14.bottom"),sQuery(id+"F0.wireOp",EDGE,"E14.top"),sQuery(id+"F0.wireOp",EDGE,"E18"),sQuery(id+"F0.wireOp",EDGE,"E19"),sQuery(id+"F0.wireOp",EDGE,"E21"),sQuery(id+"F0.wireOp",EDGE,"E22"),sQuery(id+"F0.wireOp",EDGE,"E23"),sQuery(id+"F0.wireOp",EDGE,"E24"),sQuery(id+"F0.wireOp",EDGE,"E25"),sQuery(id+"F0.wireOp",EDGE,"E26")])],"isStart":true})}),makeQuery(id+"F6.opExtrude","SWEPT_FACE",FACE,{"disambiguationData":[OSD([sQuery(id+"F5.wireOp",EDGE,"E56.left")])]})]}),makeQuery(id+"F8.opExtrude","SWEPT_FACE",FACE,{"disambiguationData":[OSD([sQuery(id+"F7.wireOp",EDGE,"E64")])]})]});
            var Q12;
            {var subQ0=sQuery(id+"F5.wireOp",EDGE,"E56.bottom");var subQ3=sQuery(id+"F5.wireOp",EDGE,"E56.right");Q12=makeQuery(id+"F8.boolean.opBoolean","SPLIT",EDGE,{"disambiguationData":[TD([makeQuery(id+"F8.opExtrude","SWEPT_FACE",FACE,{"disambiguationData":[OSD([sQuery(id+"F7.wireOp",EDGE,"E64")])]})])],"derivedFrom":makeQuery(id+"F6.opExtrude","SWEPT_EDGE",EDGE,{"disambiguationData":[OSD([subQ0,subQ3])]})});}
            var Q13;
            {var subQ0=sQuery(id+"F5.wireOp",EDGE,"E56.left");var subQ1=sQuery(id+"F5.wireOp",EDGE,"E56.bottom");Q13=makeQuery(id+"F8.boolean.opBoolean","SPLIT",EDGE,{"disambiguationData":[TD([makeQuery(id+"F8.opExtrude","SWEPT_FACE",FACE,{"disambiguationData":[OSD([sQuery(id+"F7.wireOp",EDGE,"E64")])]})])],"derivedFrom":makeQuery(id+"F6.opExtrude","SWEPT_EDGE",EDGE,{"disambiguationData":[OSD([subQ1,subQ0])]})});}
            chamfer(context, id + "F9", {"entities" : qUnion([Q0, Q1, Q2, Q3, Q4, Q5, Q6, Q7, Q8, Q9, Q10, Q11, Q12, Q13]), "width" : 1 * mm, "tangentPropagation" : true});
        }
        {
            var Q0;
            Q0=makeQuery(id+"F1.opExtrude","SWEPT_EDGE",EDGE,{"disambiguationData":[OSD([sQuery(id+"F0.wireOp",EDGE,"E28"),sQuery(id+"F0.wireOp",EDGE,"E29"),sQuery(id+"F0.wireOp",EDGE,"E32")])]});
            var Q1;
            Q1=makeQuery(id+"F1.opExtrude","SWEPT_EDGE",EDGE,{"disambiguationData":[OSD([sQuery(id+"F0.wireOp",EDGE,"E32"),sQuery(id+"F0.wireOp",EDGE,"E34")])]});
            var Q2;
            Q2=makeQuery(id+"F1.opExtrude","SWEPT_EDGE",EDGE,{"disambiguationData":[OSD([sQuery(id+"F0.wireOp",EDGE,"E30"),sQuery(id+"F0.wireOp",EDGE,"E33")])]});
            var Q3;
            Q3=makeQuery(id+"F1.opExtrude","SWEPT_EDGE",EDGE,{"disambiguationData":[OSD([sQuery(id+"F0.wireOp",EDGE,"E33"),sQuery(id+"F0.wireOp",EDGE,"E34")])]});
            fillet(context, id + "F10", {"entities" : qUnion([Q0, Q1, Q2, Q3]), "radius" : 7.48 * mm, "tangentPropagation" : true, "allowEdgeOverflow" : false});
        }
        {
            var Q0;
            Q0=makeQuery(id+"F1.opExtrude","CAP_EDGE",EDGE,{"disambiguationData":[OSD([sQuery(id+"F0.wireOp",EDGE,"E33")])],"isStart":true});
            var Q1;
            Q1=makeQuery(id+"F1.opExtrude","CAP_EDGE",EDGE,{"disambiguationData":[OSD([sQuery(id+"F0.wireOp",EDGE,"E33")])],"isStart":false});
            fillet(context, id + "F11", {"entities" : qUnion([Q0, Q1]), "radius" : 3 * mm, "tangentPropagation" : true, "allowEdgeOverflow" : false});
        }
        {
            var Q0;
            Q0=makeQuery(id+"F6.boolean.opBoolean","MERGE",FACE,{"derivedFrom":[makeQuery(id+"F1.opExtrude","CAP_FACE",FACE,{"disambiguationData":[OSD([sQuery(id+"F0.wireOp",EDGE,"E1"),sQuery(id+"F0.wireOp",EDGE,"E3.bottom"),sQuery(id+"F0.wireOp",EDGE,"E3.top"),sQuery(id+"F0.wireOp",EDGE,"E4.left"),sQuery(id+"F0.wireOp",EDGE,"E8"),sQuery(id+"F0.wireOp",EDGE,"E10"),sQuery(id+"F0.wireOp",EDGE,"E12"),sQuery(id+"F0.wireOp",EDGE,"E13"),sQuery(id+"F0.wireOp",EDGE,"E14.bottom"),sQuery(id+"F0.wireOp",EDGE,"E14.top"),sQuery(id+"F0.wireOp",EDGE,"E18"),sQuery(id+"F0.wireOp",EDGE,"E19"),sQuery(id+"F0.wireOp",EDGE,"E21"),sQuery(id+"F0.wireOp",EDGE,"E22"),sQuery(id+"F0.wireOp",EDGE,"E23"),sQuery(id+"F0.wireOp",EDGE,"E24"),sQuery(id+"F0.wireOp",EDGE,"E25"),sQuery(id+"F0.wireOp",EDGE,"E26"),sQuery(id+"F0.wireOp",EDGE,"E28"),sQuery(id+"F0.wireOp",EDGE,"E30"),sQuery(id+"F0.wireOp",EDGE,"E32"),sQuery(id+"F0.wireOp",EDGE,"E33"),sQuery(id+"F0.wireOp",EDGE,"E34"),sQuery(id+"F0.wireOp",EDGE,"E40"),sQuery(id+"F0.wireOp",EDGE,"E50"),sQuery(id+"F0.wireOp",EDGE,"E51"),sQuery(id+"F0.wireOp",EDGE,"E52"),sQuery(id+"F0.wireOp",EDGE,"E53"),sQuery(id+"F0.wireOp",EDGE,"E54"),sQuery(id+"F0.wireOp",EDGE,"E55")])],"isStart":false}),makeQuery(id+"F6.opExtrude","SWEPT_FACE",FACE,{"disambiguationData":[OSD([sQuery(id+"F5.wireOp",EDGE,"E56.right")])]})]});
            var sketch = newSketch(context, id + "F12", { "sketchPlane" : qUnion([Q0])});
            skLineSegment(sketch, "E68", {"start": v(145.54, 200.54) * mm, "end": v(227.92, 151.41) * mm});
            skLineSegment(sketch, "E69", {"start": v(227.92, 151.41) * mm, "end": v(302, -47.75) * mm});
            skLineSegment(sketch, "E70", {"start": v(302, -47.75) * mm, "end": v(-61.18, -33.01) * mm});
            skLineSegment(sketch, "E71", {"start": v(-61.18, -33.01) * mm, "end": v(145.54, 200.54) * mm});
            skSolve(sketch);
        }
        {
            var Q0;
            {var subQ49=sQuery(id+"F12.wireOp",EDGE,"E70");Q0=makeQuery(id+"F12.imprint","IMPRINT",FACE,{"disambiguationData":[TD([[makeQuery(id+"F12.imprint","IMPRINT",EDGE,{"derivedFrom":subQ49}),-1.0]])]});}
            var Q1;
            {var subQ10=sQuery(id+"F12.wireOp",EDGE,"E68");var subQ14=sQuery(id+"F12.wireOp",EDGE,"E69");var subQ15=makeQuery(id+"F12.imprint","INTERSECT",VERTEX,{"derivedFrom":[subQ10,subQ14]});Q1=makeQuery(id+"F12.imprint","IMPRINT",FACE,{"disambiguationData":[TD([[makeQuery(id+"F12.imprint","IMPRINT",EDGE,{"disambiguationData":[TD([[subQ15,1.0]])],"derivedFrom":subQ10}),-1.0]])]});}
            var Q2;
            {var subQ44=sQuery(id+"F7.wireOp",EDGE,"E63");Q2=makeQuery(id+"F12.imprint","IMPRINT",FACE,{"disambiguationData":[TD([[makeQuery(id+"F12.imprint","IMPRINT",EDGE,{"derivedFrom":makeQuery(id+"F8.boolean.opBoolean","COPY",EDGE,{"derivedFrom":makeQuery(id+"F8.opExtrude","CAP_EDGE",EDGE,{"disambiguationData":[OSD([subQ44])],"isStart":true})})}),-1.0]])]});}
            var Q3;
            {var subQ0=sQuery(id+"F0.wireOp",EDGE,"E4.left");var subQ1=sQuery(id+"F0.wireOp",EDGE,"E3.bottom");var subQ2=sQuery(id+"F0.wireOp",EDGE,"E1");var subQ3=makeQuery(id+"F1.opExtrude","CAP_FACE",FACE,{"disambiguationData":[OSD([subQ2,subQ1,sQuery(id+"F0.wireOp",EDGE,"E3.top"),subQ0,sQuery(id+"F0.wireOp",EDGE,"E8"),sQuery(id+"F0.wireOp",EDGE,"E10"),sQuery(id+"F0.wireOp",EDGE,"E12"),sQuery(id+"F0.wireOp",EDGE,"E13"),sQuery(id+"F0.wireOp",EDGE,"E14.bottom"),sQuery(id+"F0.wireOp",EDGE,"E14.top"),sQuery(id+"F0.wireOp",EDGE,"E18"),sQuery(id+"F0.wireOp",EDGE,"E19"),sQuery(id+"F0.wireOp",EDGE,"E21"),sQuery(id+"F0.wireOp",EDGE,"E22"),sQuery(id+"F0.wireOp",EDGE,"E23"),sQuery(id+"F0.wireOp",EDGE,"E24"),sQuery(id+"F0.wireOp",EDGE,"E25"),sQuery(id+"F0.wireOp",EDGE,"E26"),sQuery(id+"F0.wireOp",EDGE,"E28"),sQuery(id+"F0.wireOp",EDGE,"E30"),sQuery(id+"F0.wireOp",EDGE,"E32"),sQuery(id+"F0.wireOp",EDGE,"E33"),sQuery(id+"F0.wireOp",EDGE,"E34"),sQuery(id+"F0.wireOp",EDGE,"E40"),sQuery(id+"F0.wireOp",EDGE,"E50"),sQuery(id+"F0.wireOp",EDGE,"E51"),sQuery(id+"F0.wireOp",EDGE,"E52"),sQuery(id+"F0.wireOp",EDGE,"E53"),sQuery(id+"F0.wireOp",EDGE,"E54"),sQuery(id+"F0.wireOp",EDGE,"E55")])],"isStart":false});Q3=makeQuery(id+"F12.imprint","IMPRINT",FACE,{"disambiguationData":[TD([[makeQuery(id+"F12.imprint","IMPRINT",EDGE,{"derivedFrom":makeQuery(id+"F2.opChamfer","BLEND_EDGE",EDGE,{"blendedFrom":[makeQuery(id+"F1.opExtrude","CAP_EDGE",EDGE,{"disambiguationData":[OSD([subQ2])],"isStart":false}),subQ3],"blendedInto":[subQ3]})}),-1.0]])]});}
            extrude(context, id + "F13", {"entities" : qUnion([Q0, Q1, Q2, Q3]), "operationType" : NewBodyOperationType.REMOVE, "oppositeDirection" : true, "depth" : 25 * mm, "offsetDistance" : 25 * mm});
        }
        {
            var Q0;
            Q0=makeQuery(id+"F13.boolean.opBoolean","INTERSECT",EDGE,{"derivedFrom":[makeQuery(id+"F1.opExtrude","SWEPT_FACE",FACE,{"disambiguationData":[OSD([sQuery(id+"F0.wireOp",EDGE,"E50"),sQuery(id+"F0.wireOp",EDGE,"E51"),sQuery(id+"F0.wireOp",EDGE,"E54")])]}),makeQuery(id+"F13.opExtrude","SWEPT_FACE",FACE,{"disambiguationData":[OSD([sQuery(id+"F12.wireOp",EDGE,"E68")])]})]});
            var Q1;
            Q1=makeQuery(id+"F13.boolean.opBoolean","INTERSECT",EDGE,{"derivedFrom":[makeQuery(id+"F1.opExtrude","SWEPT_FACE",FACE,{"disambiguationData":[OSD([sQuery(id+"F0.wireOp",EDGE,"E52"),sQuery(id+"F0.wireOp",EDGE,"E53"),sQuery(id+"F0.wireOp",EDGE,"E55")])]}),makeQuery(id+"F13.opExtrude","SWEPT_FACE",FACE,{"disambiguationData":[OSD([sQuery(id+"F12.wireOp",EDGE,"E68")])]})]});
            fillet(context, id + "F14", {"entities" : qUnion([Q0, Q1]), "radius" : 5 * mm, "tangentPropagation" : true, "allowEdgeOverflow" : false});
        }
        {
            var Q0;
            {var subQ0=sQuery(id+"F0.wireOp",EDGE,"E21");var subQ1=sQuery(id+"F0.wireOp",EDGE,"E19");var subQ2=sQuery(id+"F0.wireOp",EDGE,"E23");var subQ3=sQuery(id+"F0.wireOp",EDGE,"E18");var subQ4=sQuery(id+"F0.wireOp",EDGE,"E14.top");var subQ5=sQuery(id+"F0.wireOp",EDGE,"E13");var subQ6=sQuery(id+"F0.wireOp",EDGE,"E14.bottom");var subQ7=sQuery(id+"F0.wireOp",EDGE,"E24");var subQ8=sQuery(id+"F0.wireOp",EDGE,"E12");var subQ9=sQuery(id+"F0.wireOp",EDGE,"E55");var subQ10=sQuery(id+"F0.wireOp",EDGE,"E53");var subQ11=sQuery(id+"F0.wireOp",EDGE,"E52");var subQ12=sQuery(id+"F0.wireOp",EDGE,"E22");var subQ13=sQuery(id+"F0.wireOp",EDGE,"E54");var subQ14=sQuery(id+"F0.wireOp",EDGE,"E51");var subQ15=sQuery(id+"F0.wireOp",EDGE,"E50");Q0=makeQuery(id+"F13.boolean.opBoolean","SPLIT",FACE,{"disambiguationData":[TD([makeQuery(id+"F1.opExtrude","SWEPT_FACE",FACE,{"disambiguationData":[OSD([subQ2])]})])],"derivedFrom":makeQuery(id+"F6.boolean.opBoolean","MERGE",FACE,{"derivedFrom":[makeQuery(id+"F1.opExtrude","CAP_FACE",FACE,{"disambiguationData":[OSD([sQuery(id+"F0.wireOp",EDGE,"E1"),sQuery(id+"F0.wireOp",EDGE,"E3.bottom"),sQuery(id+"F0.wireOp",EDGE,"E3.top"),sQuery(id+"F0.wireOp",EDGE,"E4.left"),sQuery(id+"F0.wireOp",EDGE,"E8"),sQuery(id+"F0.wireOp",EDGE,"E10"),subQ8,subQ5,subQ6,subQ4,subQ3,subQ1,subQ0,subQ12,subQ2,subQ7,sQuery(id+"F0.wireOp",EDGE,"E25"),sQuery(id+"F0.wireOp",EDGE,"E26"),sQuery(id+"F0.wireOp",EDGE,"E28"),sQuery(id+"F0.wireOp",EDGE,"E30"),sQuery(id+"F0.wireOp",EDGE,"E32"),sQuery(id+"F0.wireOp",EDGE,"E33"),sQuery(id+"F0.wireOp",EDGE,"E34"),sQuery(id+"F0.wireOp",EDGE,"E40"),subQ15,subQ14,subQ11,subQ10,subQ13,subQ9])],"isStart":false}),makeQuery(id+"F6.opExtrude","SWEPT_FACE",FACE,{"disambiguationData":[OSD([sQuery(id+"F5.wireOp",EDGE,"E56.right")])]})]})});}
            var sketch = newSketch(context, id + "F15", { "sketchPlane" : qUnion([Q0])});
            skCircle(sketch, "E72", {"center": v(197.6, 180.24) * mm, "radius": 5 * mm});
            skSolve(sketch);
        }
        {
            var Q0;
            Q0=makeQuery(id+"F15.imprint","IMPRINT",FACE,{"disambiguationData":[TD([[makeQuery(id+"F15.imprint","IMPRINT",EDGE,{"derivedFrom":sQuery(id+"F15.wireOp",EDGE,"E72")}),1.0]])]});
            extrude(context, id + "F16", {"entities" : qUnion([Q0]), "operationType" : NewBodyOperationType.REMOVE, "oppositeDirection" : true, "depth" : 25 * mm, "offsetDistance" : 25 * mm});
        }
        {
            var Q0;
            {var subQ0=sQuery(id+"F0.wireOp",EDGE,"E21");var subQ1=sQuery(id+"F0.wireOp",EDGE,"E19");var subQ2=sQuery(id+"F0.wireOp",EDGE,"E23");var subQ3=sQuery(id+"F0.wireOp",EDGE,"E18");var subQ4=sQuery(id+"F0.wireOp",EDGE,"E14.top");var subQ5=sQuery(id+"F0.wireOp",EDGE,"E13");var subQ6=sQuery(id+"F0.wireOp",EDGE,"E14.bottom");var subQ7=sQuery(id+"F0.wireOp",EDGE,"E24");var subQ8=sQuery(id+"F0.wireOp",EDGE,"E12");var subQ9=sQuery(id+"F0.wireOp",EDGE,"E55");var subQ10=sQuery(id+"F0.wireOp",EDGE,"E53");var subQ11=sQuery(id+"F0.wireOp",EDGE,"E52");var subQ12=sQuery(id+"F0.wireOp",EDGE,"E22");var subQ13=sQuery(id+"F0.wireOp",EDGE,"E54");var subQ14=sQuery(id+"F0.wireOp",EDGE,"E51");var subQ15=sQuery(id+"F0.wireOp",EDGE,"E50");Q0=makeQuery(id+"F13.boolean.opBoolean","SPLIT",FACE,{"disambiguationData":[TD([makeQuery(id+"F1.opExtrude","SWEPT_FACE",FACE,{"disambiguationData":[OSD([subQ2])]})])],"derivedFrom":makeQuery(id+"F6.boolean.opBoolean","MERGE",FACE,{"derivedFrom":[makeQuery(id+"F1.opExtrude","CAP_FACE",FACE,{"disambiguationData":[OSD([sQuery(id+"F0.wireOp",EDGE,"E1"),sQuery(id+"F0.wireOp",EDGE,"E3.bottom"),sQuery(id+"F0.wireOp",EDGE,"E3.top"),sQuery(id+"F0.wireOp",EDGE,"E4.left"),sQuery(id+"F0.wireOp",EDGE,"E8"),sQuery(id+"F0.wireOp",EDGE,"E10"),subQ8,subQ5,subQ6,subQ4,subQ3,subQ1,subQ0,subQ12,subQ2,subQ7,sQuery(id+"F0.wireOp",EDGE,"E25"),sQuery(id+"F0.wireOp",EDGE,"E26"),sQuery(id+"F0.wireOp",EDGE,"E28"),sQuery(id+"F0.wireOp",EDGE,"E30"),sQuery(id+"F0.wireOp",EDGE,"E32"),sQuery(id+"F0.wireOp",EDGE,"E33"),sQuery(id+"F0.wireOp",EDGE,"E34"),sQuery(id+"F0.wireOp",EDGE,"E40"),subQ15,subQ14,subQ11,subQ10,subQ13,subQ9])],"isStart":false}),makeQuery(id+"F6.opExtrude","SWEPT_FACE",FACE,{"disambiguationData":[OSD([sQuery(id+"F5.wireOp",EDGE,"E56.right")])]})]})});}
            var sketch = newSketch(context, id + "F17", { "sketchPlane" : qUnion([Q0])});
            skArc(sketch, "E73", {"start": v(338.65, 228.46) * mm, "mid": v(339.52, 219.39) * mm, "end": v(347.23, 214.53) * mm});
            skSolve(sketch);
        }
        {
            var Q0;
            Q0 = qSketchRegion(id + "F17", true);
            var Q1;
            {var subQ7=sQuery(id+"F17.wireOp",EDGE,"E73");Q1=makeQuery(id+"F17.imprint","IMPRINT",FACE,{"disambiguationData":[TD([[makeQuery(id+"F17.imprint","IMPRINT",EDGE,{"derivedFrom":subQ7}),1.0]])]});}
            extrude(context, id + "F18", {"entities" : qUnion([Q0, Q1]), "operationType" : NewBodyOperationType.ADD, "depth" : 5 * mm, "offsetDistance" : 25 * mm});
        }
        {
            var Q0;
            {var subQ0=sQuery(id+"F0.wireOp",EDGE,"E19");var subQ1=sQuery(id+"F0.wireOp",EDGE,"E18");var subQ2=sQuery(id+"F0.wireOp",EDGE,"E14.top");var subQ3=sQuery(id+"F0.wireOp",EDGE,"E13");var subQ4=sQuery(id+"F0.wireOp",EDGE,"E14.bottom");var subQ5=sQuery(id+"F0.wireOp",EDGE,"E23");var subQ6=sQuery(id+"F0.wireOp",EDGE,"E24");var subQ7=sQuery(id+"F0.wireOp",EDGE,"E21");var subQ8=sQuery(id+"F0.wireOp",EDGE,"E55");var subQ9=sQuery(id+"F0.wireOp",EDGE,"E53");var subQ10=sQuery(id+"F0.wireOp",EDGE,"E52");var subQ11=sQuery(id+"F0.wireOp",EDGE,"E12");var subQ12=sQuery(id+"F0.wireOp",EDGE,"E22");var subQ13=sQuery(id+"F0.wireOp",EDGE,"E54");var subQ14=sQuery(id+"F0.wireOp",EDGE,"E51");var subQ15=sQuery(id+"F0.wireOp",EDGE,"E50");Q0=makeQuery(id+"F13.boolean.opBoolean","SPLIT",FACE,{"disambiguationData":[TD([makeQuery(id+"F1.opExtrude","SWEPT_FACE",FACE,{"disambiguationData":[OSD([subQ5])]})])],"derivedFrom":makeQuery(id+"F6.boolean.opBoolean","MERGE",FACE,{"derivedFrom":[makeQuery(id+"F1.opExtrude","CAP_FACE",FACE,{"disambiguationData":[OSD([sQuery(id+"F0.wireOp",EDGE,"E1"),sQuery(id+"F0.wireOp",EDGE,"E3.bottom"),sQuery(id+"F0.wireOp",EDGE,"E3.top"),sQuery(id+"F0.wireOp",EDGE,"E4.left"),sQuery(id+"F0.wireOp",EDGE,"E8"),sQuery(id+"F0.wireOp",EDGE,"E10"),subQ11,subQ3,subQ4,subQ2,subQ1,subQ0,subQ7,subQ12,subQ5,subQ6,sQuery(id+"F0.wireOp",EDGE,"E25"),sQuery(id+"F0.wireOp",EDGE,"E26"),sQuery(id+"F0.wireOp",EDGE,"E28"),sQuery(id+"F0.wireOp",EDGE,"E30"),sQuery(id+"F0.wireOp",EDGE,"E32"),sQuery(id+"F0.wireOp",EDGE,"E33"),sQuery(id+"F0.wireOp",EDGE,"E34"),sQuery(id+"F0.wireOp",EDGE,"E40"),subQ15,subQ14,subQ10,subQ9,subQ13,subQ8])],"isStart":true}),makeQuery(id+"F6.opExtrude","SWEPT_FACE",FACE,{"disambiguationData":[OSD([sQuery(id+"F5.wireOp",EDGE,"E56.left")])]})]})});}
            var sketch = newSketch(context, id + "F19", { "sketchPlane" : qUnion([Q0])});
            skPoint(sketch, "E74", {"position": v(-338.65, 228.46) * mm});
            skArc(sketch, "E75", {"start": v(-347.36, 214.58) * mm, "mid": v(-339.6, 219.38) * mm, "end": v(-338.65, 228.46) * mm});
            skSolve(sketch);
        }
        {
            var Q0;
            Q0 = qSketchRegion(id + "F19", true);
            var Q1;
            {var subQ7=sQuery(id+"F19.wireOp",EDGE,"E75");Q1=makeQuery(id+"F19.imprint","IMPRINT",FACE,{"disambiguationData":[TD([[makeQuery(id+"F19.imprint","IMPRINT",EDGE,{"derivedFrom":subQ7}),1.0]])]});}
            extrude(context, id + "F20", {"entities" : qUnion([Q0, Q1]), "operationType" : NewBodyOperationType.ADD, "depth" : 5 * mm, "offsetDistance" : 25 * mm});
        }
    });
